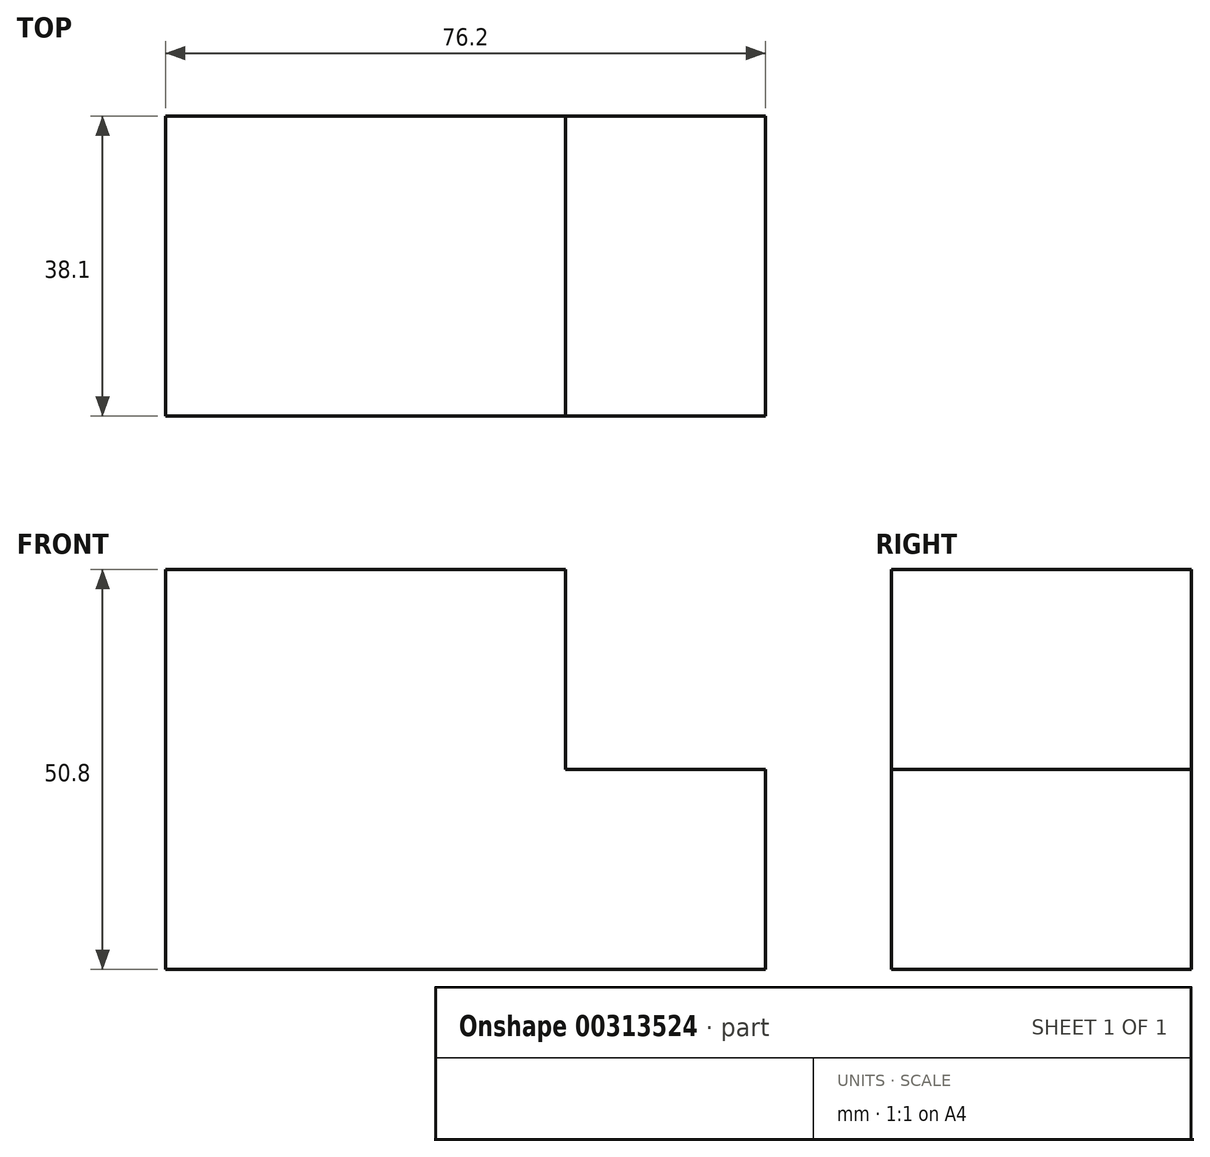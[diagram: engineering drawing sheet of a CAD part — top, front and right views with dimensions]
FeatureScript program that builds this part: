
annotation { "Feature Type Name" : "Feature", "Feature Type Description" : "" }
export const myFeature = defineFeature(function(context is Context, id is Id, definition is map)
    precondition{}
    {
        {
            var Q0;
            Q0=qCreatedBy(makeId("Front.planeOp"),FACE);
            var sketch = newSketch(context, id + "F0", { "sketchPlane" : qUnion([Q0])});
            skLineSegment(sketch, "E0", {"start": v(-32.6, 18.24) * mm, "end": v(-32.6, -32.56) * mm});
            skLineSegment(sketch, "E1", {"start": v(-32.6, -32.56) * mm, "end": v(43.6, -32.56) * mm});
            skLineSegment(sketch, "E2", {"start": v(43.6, -32.56) * mm, "end": v(43.6, -7.16) * mm});
            skLineSegment(sketch, "E3", {"start": v(43.6, -7.16) * mm, "end": v(18.2, -7.16) * mm});
            skLineSegment(sketch, "E4", {"start": v(18.2, -7.16) * mm, "end": v(18.2, 18.24) * mm});
            skLineSegment(sketch, "E5", {"start": v(18.2, 18.24) * mm, "end": v(-32.6, 18.24) * mm});
            skSolve(sketch);
        }
        {
            var Q0;
            Q0=makeQuery(id+"F0.imprint","IMPRINT",FACE,{"disambiguationData":[TD([[makeQuery(id+"F0.imprint","IMPRINT",EDGE,{"derivedFrom":sQuery(id+"F0.wireOp",EDGE,"E0")}),1.0]])]});
            extrude(context, id + "F1", {"entities" : qUnion([Q0]), "depth" : 38.1 * mm});
        }
    });
